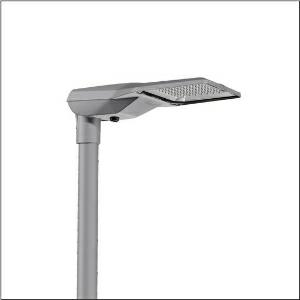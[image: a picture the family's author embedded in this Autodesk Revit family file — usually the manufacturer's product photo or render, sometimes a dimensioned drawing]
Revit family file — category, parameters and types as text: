
# Revit family: streetlight_sl_21_midi___st1_0ab_5xe3m33r08mb_c7ee
name_source: partatom
category: Lighting Fixtures
units: mm (PartAtom-declared; Revit-internal decimal feet)

## family parameters
Cut with Voids When Loaded = No
Host = Face
Light Source = No
Part Type = Normal
Room Calculation Point = No
Round Connector Dimension = Use Diameter
Shared = No

## types (1)
- --- (1 x LED, 16080 lm, 136 W, 3000K)
    Apparent Load = 136 VA
    CIE Flux Codes = 38 73 97 100 100
    Color Rendering = 70
    Color Temperature = 3000K
    Default Elevation = 1800 mm
    Description = Streetlight SL 21 midi, mast luminaire, primary light control with lens, of PMMA, primary optical cover: cover, of toughened safety glass, transparent, light distribution: ST1.0aB, light emission: direct distribution, primary light characteristic: asymmetric, installation type: side-entry, post-top, LED, High Power LED, rated luminous flux: 16.080lm, luminous efficacy: 118lm/W, light colour: 730, colour temperature: 3000K, control gear: D4i, control: flexible luminous flux parameterisation, time-dependent luminous flux control, constant luminous flux control, overheat protection, pre-setting: logarithmic dimming characteristic, mains connection: 230..240V, AC, 50/60Hz, start of lifetime: 136W, end of service life: 142W, reduction: 61W, luminaire housing, of diecast aluminium, powder-coated, SITECO metallic grey (DB 702S), corrosivity category C5 high according to DIN EN ISO 12944, please order mast flange separately, inclination adjustable: 0°, 5°, 10°, 15°, sealing non-destructively replaceable, multi-level sealing system, length: 644mm, width: 335mm, height: 110mm, mast flange for spigot size: 42mm (side-entry): 5XC10008XM4, 60/48mm (side-entry/post-top): 5XC10108XM2, 76/60mm (side-entry/post-top): 5XC10108XM1, mounting height: 4..8m, Smart Interface below, protection rating (complete): IP66, insulation class (complete): insulation class II (safety insulation), certification: CE, ENEC, ENEC+, VDE, impact resistance: IK10, permissible operating ambient temperature for outdoor applications: -40..+50°C, standard-compliant lighting for roads and squares, packaging unit: 1 piece

Light Distribution: ST1.0aB
    Height = 111 mm
    Lamp = 1 x LED
    Lamp Light Flux = 16080 lm
    Lamp Power = 136 W
    Lamp count = 1
    Length = 644 mm
    Luminous efficacy = 118 lm/W
    Manufacturer = Siteco
    ModVariant = No
    Model = 5XE3M33R08MB
    Number of Poles = 1
    OnlyDefault = Yes
    Power Factor = 1
    Product Name = Streetlight SL 21 midi | ST1.0aB
    Product group = mast luminaire | pylon top
    ProductGroupID = 6100
    Protection Class = Protection class II
    Protection Degree = IP 66
    RLX_Detail_Level = 1
    RLX_Emergency_Light_Flux = 0 lm
    RLX_Emergency_Type = 0
    RLX_Emergency_Type_DB = No
    RlxData = <blob elided: 26973 chars, md5=7b22504a>
    Socket = socket
    Standby Power = 0 W
    System Light Flux = 16081 lm
    System Power = 136 W
    Type Comments = factory setting: luminous flux: 100 % | dim-lin: 254 | 695 mA
    Type Image = l_1004300.jpg
    URL = http://relux.com
    VarID = @adj_180423
    Voltage = 0 V
    Weight = 0.00 kg
    Width = 336 mm

## geometry (parser evidence)
native form markers: Blend x4, Sweep x11
no freeform markers — native parametric forms only
